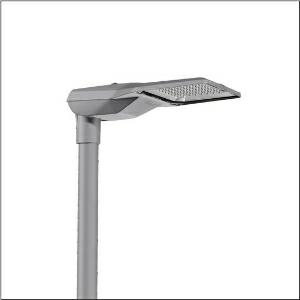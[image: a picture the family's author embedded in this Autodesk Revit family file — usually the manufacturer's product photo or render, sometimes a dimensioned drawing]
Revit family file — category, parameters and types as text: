
# Revit family: streetlight_sl_21_midi___p0_8ab_5xe3r33s08nb_ccbb
name_source: partatom
category: Lighting Fixtures
units: mm (PartAtom-declared; Revit-internal decimal feet)

## family parameters
Cut with Voids When Loaded = No
Host = Face
Light Source = No
Part Type = Normal
Room Calculation Point = No
Round Connector Dimension = Use Diameter
Shared = No

## types (1)
- --- (1 x LED, 19710 lm, 151.2 W, 3000K)
    Apparent Load = 151 VA
    CIE Flux Codes = 39 72 97 100 100
    Color Rendering = 70
    Color Temperature = 3000K
    Default Elevation = 1800 mm
    Description = Streetlight SL 21 midi, mast luminaire, primary light control with lens, of PMMA, primary optical cover: cover, of toughened safety glass, transparent, light distribution: P0.8aB, light emission: direct distribution, primary light characteristic: asymmetric, installation type: post-top, side-entry, LED, High Power LED, rated luminous flux: 19.710lm, luminous efficacy: 130lm/W, light colour: 730, colour temperature: 3000K, control gear: D4i, control: pre-setting: logarithmic dimming characteristic, flexible luminous flux parameterisation, time-dependent luminous flux control, constant luminous flux control, overheat protection, mains connection: 230..240V, AC, 50/60Hz, start of lifetime: 151W, end of service life: 157W, reduction: 70W, luminaire housing, of diecast aluminium, powder-coated, Siteco® metallic grey (DB 702S), corrosivity category C5 mid according to DIN EN ISO 12944, multi-level sealing system, sealing non-destructively replaceable, inclination adjustable: 0°, 5°, 10°, 15°, please order mast flange separately, length: 644mm, width: 335mm, height: 110mm, mast flange for spigot size: 42mm (side-entry): 5XC10008XM4, 60/48mm (side-entry/post-top): 5XC10108XM2, 76/60mm (side-entry/post-top): 5XC10108XM1, mounting height: 4..8m, Smart Interface above, protection rating (complete): IP66, insulation class (complete): insulation class II (safety insulation), certification: CE, ENEC, ENEC+, VDE, impact resistance: IK10, permissible operating ambient temperature for outdoor applications: -40..+50°C, standard-compliant lighting for roads and squares, packaging unit: 1 piece

Light Distribution: P0.8aB
    Height = 111 mm
    Lamp = 1 x LED
    Lamp Light Flux = 19710 lm
    Lamp Power = 151.2 W
    Lamp count = 1
    Length = 644 mm
    Luminous efficacy = 130 lm/W
    Manufacturer = Siteco
    ModVariant = No
    Model = 5XE3R33S08NB
    Number of Poles = 1
    OnlyDefault = Yes
    Power Factor = 1
    Product Name = Streetlight SL 21 midi | P0.8aB
    Product group = mast luminaire | pylon top
    ProductGroupID = 6100
    Protection Class = Protection class II
    Protection Degree = IP 66
    RLX_Detail_Level = 1
    RLX_Emergency_Light_Flux = 0 lm
    RLX_Emergency_Type = 0
    RLX_Emergency_Type_DB = No
    RlxData = <blob elided: 26581 chars, md5=7d5873ce>
    Socket = socket
    Standby Power = 0 W
    System Light Flux = 19710 lm
    System Power = 151 W
    Type Comments = factory setting: luminous flux: 100 % | dim-lin: 254 | 802 mA
    Type Image = l_1004302.jpg
    URL = http://relux.com
    VarID = @adj_070942
    Voltage = 0 V
    Weight = 0.00 kg
    Width = 336 mm

## geometry (parser evidence)
native form markers: Blend x4, Sweep x11
no freeform markers — native parametric forms only
